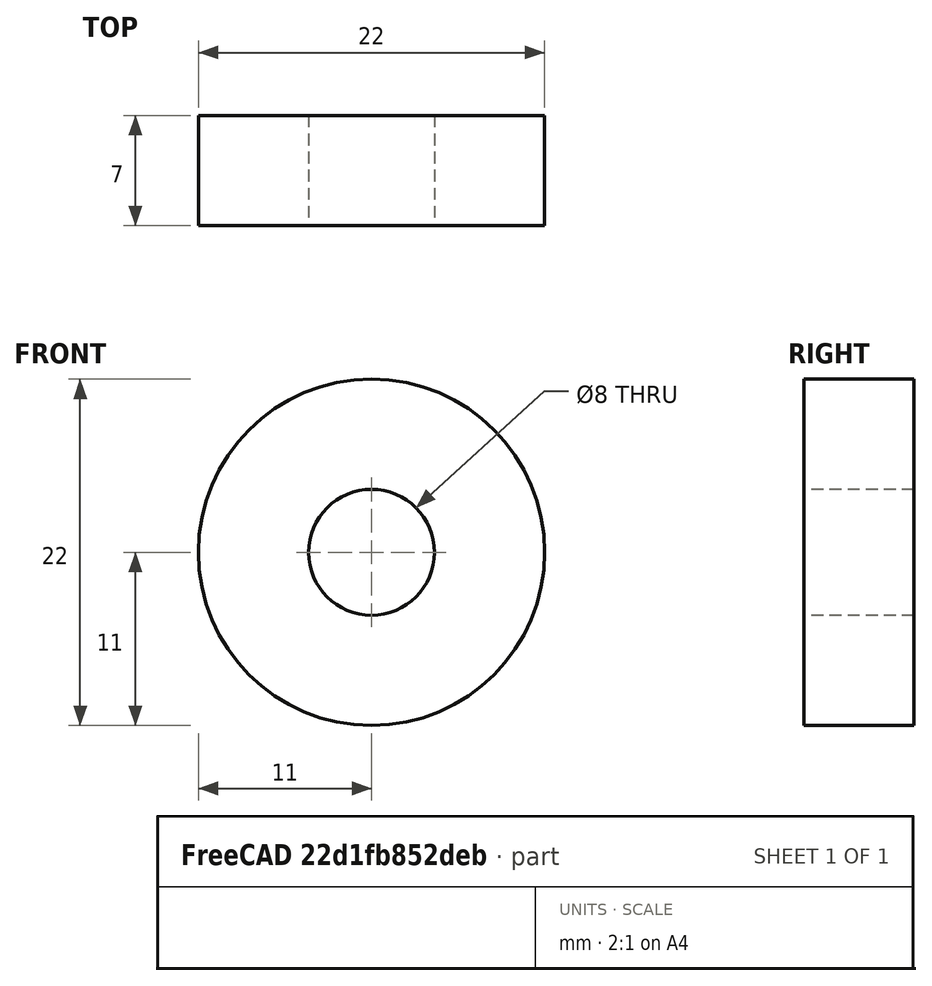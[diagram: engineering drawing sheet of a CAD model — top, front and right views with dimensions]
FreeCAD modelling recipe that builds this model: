
FCSTD DOCUMENT  (FreeCAD 0.21R33668 +7 (Git))
Label: 608
License: All rights reserved
LicenseURL: https://en.wikipedia.org/wiki/All_rights_reserved
objects: Sketcher::SketchObject×1, PartDesign::Revolution×1, PartDesign::Body×1
note: 4 computed .brp shape members not serialized (recipe doc carries the construction recipe); baked Part::Feature solids carry a one-line shape summary decoded from their .brp

FEATURE [Sketcher::SketchObject] Sketch
  FullyConstrained = true
  MapMode = 5
  Placement = pos=(0,0,0) rot=(0.57735,0.57735,0.57735;2.0944rad)
  Support = -> [YZ_Plane]
  sketch-geometry (4):
    g0: LineSegment StartX=-3.5 StartY=11 StartZ=0 EndX=3.5 EndY=11 EndZ=0
    g1: LineSegment StartX=3.5 StartY=11 StartZ=0 EndX=3.5 EndY=4 EndZ=0
    g2: LineSegment StartX=3.5 StartY=4 StartZ=0 EndX=-3.5 EndY=4 EndZ=0
    g3: LineSegment StartX=-3.5 StartY=4 StartZ=0 EndX=-3.5 EndY=11 EndZ=0
  constraints (11):
    c: Coincident(g0,g1)
    c: Coincident(g1,g2)
    c: Coincident(g2,g3)
    c: Coincident(g3,g0)
    c: Horizontal(g2)
    c: Vertical(g1)
    c: Vertical(g3)
    c: Symmetric(g0,g0,g-2)
    c: DistanceX(g0,g0) = 7
    c: DistanceY(g-1,g2) = 4
    c: DistanceY(g-1,g0) = 11
FEATURE [PartDesign::Revolution] Revolution
  Angle = 360
  Axis = (3e-16,1,-2e-16)
  Base = (0,0,0)
  Placement = pos=(0,0,0) rot=(1,1,1;2.0944rad)
  Profile = -> Sketch
  ReferenceAxis = -> Sketch [H_Axis]
FEATURE [PartDesign::Body] Body  label="608"
  Group = -> [Sketch,Revolution]
  Origin = -> Origin
  Tip = -> Revolution
